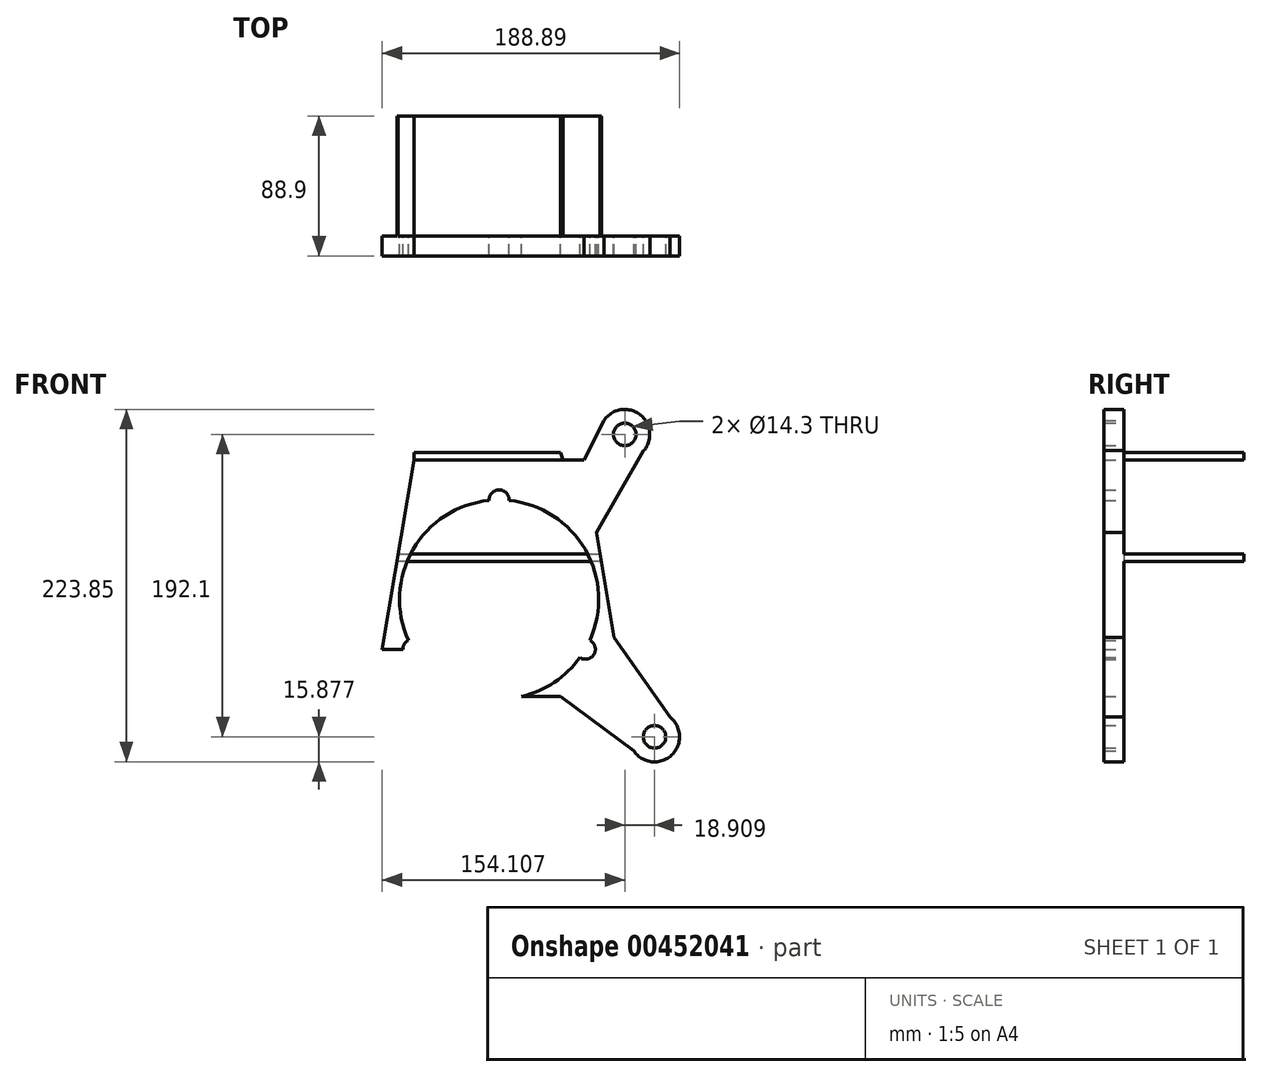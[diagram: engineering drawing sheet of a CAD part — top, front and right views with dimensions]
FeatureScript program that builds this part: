
annotation { "Feature Type Name" : "Feature", "Feature Type Description" : "" }
export const myFeature = defineFeature(function(context is Context, id is Id, definition is map)
    precondition{}
    {
        {
            var Q0;
            Q0=qCreatedBy(makeId("Front.planeOp"),FACE);
            var sketch = newSketch(context, id + "F0", { "sketchPlane" : qUnion([Q0])});
            skLineSegment(sketch, "E0", {"start": v(-53.98, 0) * mm, "end": v(53.98, 0) * mm});
            skLineSegment(sketch, "E1", {"start": v(-79.37, -150.27) * mm, "end": v(79.38, -150.27) * mm});
            skLineSegment(sketch, "E2", {"start": v(-53.97, 0) * mm, "end": v(-79.37, -150.27) * mm});
            skLineSegment(sketch, "E3", {"start": v(53.97, 0) * mm, "end": v(79.38, -150.27) * mm});
            skCircle(sketch, "E4", {"center": v(0, -25.4) * mm, "radius": 6.35 * mm});
            skCircle(sketch, "E5", {"center": v(-54.77, -120.26) * mm, "radius": 6.35 * mm});
            skCircle(sketch, "E6", {"center": v(54.77, -120.26) * mm, "radius": 6.35 * mm});
            skCircle(sketch, "E7", {"center": v(0, -88.67) * mm, "radius": 49.21 * mm});
            skLineSegment(sketch, "E8", {"start": v(-54.77, -120.26) * mm, "end": v(-156.37, -120.26) * mm});
            skLineSegment(sketch, "E9", {"start": v(0, -150.27) * mm, "end": v(0, -61.37) * mm});
            skLineSegment(sketch, "E10", {"start": v(-156.37, -120.26) * mm, "end": v(-156.37, -15.35) * mm});
            skCircle(sketch, "E11", {"center": v(0, -88.67) * mm, "radius": 131.75 * mm});
            skCircle(sketch, "E12", {"center": v(79.8, 16.17) * mm, "radius": 7.15 * mm});
            skCircle(sketch, "E13", {"center": v(98.72, -175.93) * mm, "radius": 7.15 * mm});
            skCircle(sketch, "E14", {"center": v(98.72, -175.93) * mm, "radius": 15.88 * mm});
            skCircle(sketch, "E15", {"center": v(79.8, 16.17) * mm, "radius": 15.88 * mm});
            skLineSegment(sketch, "E16", {"start": v(91.84, 5.8) * mm, "end": v(61.78, -46.18) * mm});
            skLineSegment(sketch, "E17", {"start": v(108.5, -163.43) * mm, "end": v(73.02, -112.66) * mm});
            skLineSegment(sketch, "E18", {"start": v(85.59, -184.86) * mm, "end": v(39.06, -150.27) * mm});
            skLineSegment(sketch, "E19", {"start": v(66.62, 25) * mm, "end": v(53.98, 0) * mm});
            skCircle(sketch, "E20", {"center": v(0, -88.67) * mm, "radius": 63.22 * mm});
            skSolve(sketch);
        }
        {
            var Q0;
            {var subQ5=sQuery(id+"F0.wireOp",EDGE,"E0");Q0=makeQuery(id+"F0.imprint","IMPRINT",FACE,{"disambiguationData":[TD([[makeQuery(id+"F0.imprint","IMPRINT",EDGE,{"derivedFrom":subQ5}),-1.0]])]});}
            var Q1;
            {var subQ3=sQuery(id+"F0.wireOp",EDGE,"E16");Q1=makeQuery(id+"F0.imprint","IMPRINT",FACE,{"disambiguationData":[TD([[makeQuery(id+"F0.imprint","IMPRINT",EDGE,{"derivedFrom":subQ3}),-1.0]])]});}
            var Q2;
            {var subQ0=sQuery(id+"F0.wireOp",EDGE,"E12");var subQ1=sQuery(id+"F0.wireOp",EDGE,"E11");var subQ2=makeQuery(id+"F0.imprint","INTERSECT",VERTEX,{"disambiguationData":[OD(0.0)],"derivedFrom":[subQ1,subQ0]});Q2=makeQuery(id+"F0.imprint","IMPRINT",FACE,{"disambiguationData":[TD([[makeQuery(id+"F0.imprint","IMPRINT",EDGE,{"disambiguationData":[TD([[subQ2,1.0]])],"derivedFrom":subQ0}),-1.0]])]});}
            var Q3;
            {var subQ1=sQuery(id+"F0.wireOp",EDGE,"E11");var subQ3=sQuery(id+"F0.wireOp",EDGE,"E12");var subQ4=makeQuery(id+"F0.imprint","INTERSECT",VERTEX,{"disambiguationData":[OD(0.0)],"derivedFrom":[subQ1,subQ3]});Q3=makeQuery(id+"F0.imprint","IMPRINT",FACE,{"disambiguationData":[TD([[makeQuery(id+"F0.imprint","IMPRINT",EDGE,{"disambiguationData":[TD([[subQ4,-1.0]])],"derivedFrom":subQ3}),-1.0]])]});}
            var Q4;
            {var subQ0=sQuery(id+"F0.wireOp",EDGE,"E17");Q4=makeQuery(id+"F0.imprint","IMPRINT",FACE,{"disambiguationData":[TD([[makeQuery(id+"F0.imprint","IMPRINT",EDGE,{"derivedFrom":subQ0}),1.0]])]});}
            var Q5;
            {var subQ0=sQuery(id+"F0.wireOp",EDGE,"E14");var subQ1=sQuery(id+"F0.wireOp",EDGE,"E11");var subQ7=makeQuery(id+"F0.imprint","INTERSECT",VERTEX,{"derivedFrom":[subQ1,subQ0]});Q5=makeQuery(id+"F0.imprint","IMPRINT",FACE,{"disambiguationData":[TD([[makeQuery(id+"F0.imprint","IMPRINT",EDGE,{"disambiguationData":[TD([[subQ7,-1.0]])],"derivedFrom":subQ1}),1.0]])]});}
            var Q6;
            {var subQ0=sQuery(id+"F0.wireOp",EDGE,"E14");var subQ1=sQuery(id+"F0.wireOp",EDGE,"E11");var subQ2=makeQuery(id+"F0.imprint","INTERSECT",VERTEX,{"derivedFrom":[subQ1,subQ0]});Q6=makeQuery(id+"F0.imprint","IMPRINT",FACE,{"disambiguationData":[TD([[makeQuery(id+"F0.imprint","IMPRINT",EDGE,{"disambiguationData":[TD([[subQ2,-1.0]])],"derivedFrom":subQ1}),-1.0]])]});}
            extrude(context, id + "F1", {"entities" : qUnion([Q0, Q1, Q2, Q3, Q4, Q5, Q6]), "depth" : 6.35 * mm, "hasSecondDirection" : true, "secondDirectionOppositeDirection" : true, "secondDirectionDepth" : 6.35 * mm});
        }
        {
            var Q0;
            Q0=makeQuery(id+"FOitl75tAzy8YSx_1.boolean.opBoolean","MERGE",FACE,{"derivedFrom":[makeQuery(id+"F1.opExtrude","CAP_FACE",FACE,{"disambiguationData":[OSD([sQuery(id+"F0.wireOp",EDGE,"E0"),sQuery(id+"F0.wireOp",EDGE,"E1"),sQuery(id+"F0.wireOp",EDGE,"E2"),sQuery(id+"F0.wireOp",EDGE,"E3"),sQuery(id+"F0.wireOp",EDGE,"E4"),sQuery(id+"F0.wireOp",EDGE,"E5"),sQuery(id+"F0.wireOp",EDGE,"E6"),sQuery(id+"F0.wireOp",EDGE,"E7"),sQuery(id+"F0.wireOp",EDGE,"E12"),sQuery(id+"F0.wireOp",EDGE,"E13"),sQuery(id+"F0.wireOp",EDGE,"E14"),sQuery(id+"F0.wireOp",EDGE,"E15"),sQuery(id+"F0.wireOp",EDGE,"E16"),sQuery(id+"F0.wireOp",EDGE,"E17"),sQuery(id+"F0.wireOp",EDGE,"E18"),sQuery(id+"F0.wireOp",EDGE,"E19")])],"isStart":true}),makeQuery(id+"FOitl75tAzy8YSx_1.opExtrude","SWEPT_FACE",FACE,{"disambiguationData":[OSD([sQuery(id+"FF2iT7GUfIGANON_1.wireOp",EDGE,"4CpptAuS-EF7Z-popT-YOGi-WrK1huyTGHxH.top")])]})]});
            var sketch = newSketch(context, id + "F2", { "sketchPlane" : qUnion([Q0])});
            skLineSegment(sketch, "E21.bottom", {"start": v(53.98, 0) * mm, "end": v(-39.06, 0) * mm});
            skLineSegment(sketch, "E21.top", {"start": v(53.98, 4.75) * mm, "end": v(-39.06, 4.75) * mm});
            skLineSegment(sketch, "E21.left", {"start": v(53.98, 0) * mm, "end": v(53.98, 4.75) * mm});
            skLineSegment(sketch, "E21.right", {"start": v(-39.06, 0) * mm, "end": v(-39.06, 4.75) * mm});
            skLineSegment(sketch, "E22", {"start": v(-39.06, 0) * mm, "end": v(-81.74, -125.14) * mm});
            skLineSegment(sketch, "E23", {"start": v(-81.74, -125.14) * mm, "end": v(-79.02, -121.24) * mm});
            skLineSegment(sketch, "E24", {"start": v(-79.02, -121.24) * mm, "end": v(-39.06, 4.75) * mm});
            skSolve(sketch);
        }
        {
            var Q0;
            Q0=makeQuery(id+"F2.imprint","IMPRINT",FACE,{"disambiguationData":[TD([[makeQuery(id+"F2.imprint","IMPRINT",EDGE,{"derivedFrom":sQuery(id+"F2.wireOp",EDGE,"E21.right")}),1.0]])]});
            var Q1;
            {var subQ0=sQuery(id+"F2.wireOp",EDGE,"E21.bottom");Q1=makeQuery(id+"F2.imprint","IMPRINT",FACE,{"disambiguationData":[TD([[makeQuery(id+"F2.imprint","IMPRINT",EDGE,{"derivedFrom":subQ0}),-1.0]])]});}
            extrude(context, id + "F3", {"entities" : qUnion([Q0, Q1]), "operationType" : NewBodyOperationType.ADD, "depth" : 76.2 * mm});
        }
        {
            var Q0;
            Q0=makeQuery(id+"F3.opExtrude","SWEPT_FACE",FACE,{"disambiguationData":[OSD([sQuery(id+"F2.wireOp",EDGE,"E21.top")])]});
            var sketch = newSketch(context, id + "F4", { "sketchPlane" : qUnion([Q0])});
            skCircle(sketch, "E25", {"center": v(0, 46.65) * mm, "radius": 9.53 * mm});
            skSolve(sketch);
        }
        {
            var Q0;
            Q0=sQuery(id+"F4.wireOp",VERTEX,"E25.center");
            var Q1;
            Q1=makeQuery(id+"F1.opExtrude","SWEPT_BODY",BODY,{"disambiguationData":[OSD([sQuery(id+"F0.wireOp",EDGE,"E0"),sQuery(id+"F0.wireOp",EDGE,"E1"),sQuery(id+"F0.wireOp",EDGE,"E2"),sQuery(id+"F0.wireOp",EDGE,"E3"),sQuery(id+"F0.wireOp",EDGE,"E4"),sQuery(id+"F0.wireOp",EDGE,"E5"),sQuery(id+"F0.wireOp",EDGE,"E6"),sQuery(id+"F0.wireOp",EDGE,"E7"),sQuery(id+"F0.wireOp",EDGE,"E12"),sQuery(id+"F0.wireOp",EDGE,"E13"),sQuery(id+"F0.wireOp",EDGE,"E14"),sQuery(id+"F0.wireOp",EDGE,"E15"),sQuery(id+"F0.wireOp",EDGE,"E16"),sQuery(id+"F0.wireOp",EDGE,"E17"),sQuery(id+"F0.wireOp",EDGE,"E18"),sQuery(id+"F0.wireOp",EDGE,"E19")])]});
            hole(context, id + "F5", {"style" : HoleStyle.SIMPLE, "endStyle" : HoleEndStyle.THROUGH, "holeDiameter" : 19.05 * mm, "isTappedThrough" : true, "tappedDepth" : 12.7 * mm, "tapClearance" : 3, "locations" : qUnion([Q0]), "scope" : qUnion([Q1])});
        }
        {
            var Q0;
            {var subQ0=sQuery(id+"F0.wireOp",EDGE,"E16");var subQ1=sQuery(id+"F0.wireOp",EDGE,"E15");var subQ2=sQuery(id+"F0.wireOp",EDGE,"E12");var subQ3=sQuery(id+"F0.wireOp",EDGE,"E7");var subQ5=sQuery(id+"F0.wireOp",EDGE,"E6");var subQ7=sQuery(id+"F0.wireOp",EDGE,"E17");var subQ8=sQuery(id+"F0.wireOp",EDGE,"E2");var subQ9=sQuery(id+"F0.wireOp",EDGE,"E3");var subQ10=sQuery(id+"F0.wireOp",EDGE,"E4");var subQ11=sQuery(id+"FF2iT7GUfIGANON_1.wireOp",EDGE,"4CpptAuS-EF7Z-popT-YOGi-WrK1huyTGHxH.top");var subQ12=sQuery(id+"F0.wireOp",EDGE,"E5");var subQ13=sQuery(id+"F0.wireOp",EDGE,"E19");Q0=makeQuery(id+"F3.boolean.opBoolean","SPLIT",FACE,{"disambiguationData":[TD([makeQuery(id+"F1.opExtrude","SWEPT_FACE",FACE,{"disambiguationData":[OSD([subQ8])]})])],"derivedFrom":makeQuery(id+"FOitl75tAzy8YSx_1.boolean.opBoolean","MERGE",FACE,{"derivedFrom":[makeQuery(id+"F1.opExtrude","CAP_FACE",FACE,{"disambiguationData":[OSD([sQuery(id+"F0.wireOp",EDGE,"E0"),sQuery(id+"F0.wireOp",EDGE,"E1"),subQ8,subQ9,subQ10,subQ12,subQ5,subQ3,subQ2,sQuery(id+"F0.wireOp",EDGE,"E13"),sQuery(id+"F0.wireOp",EDGE,"E14"),subQ1,subQ0,subQ7,sQuery(id+"F0.wireOp",EDGE,"E18"),subQ13])],"isStart":true}),makeQuery(id+"FOitl75tAzy8YSx_1.opExtrude","SWEPT_FACE",FACE,{"disambiguationData":[OSD([subQ11])]})]})});}
            var sketch = newSketch(context, id + "F6", { "sketchPlane" : qUnion([Q0])});
            skLineSegment(sketch, "E26", {"start": v(0, -64.57) * mm, "end": v(64.89, -64.57) * mm});
            skLineSegment(sketch, "E27", {"start": v(64.89, -64.57) * mm, "end": v(64.1, -59.89) * mm});
            skLineSegment(sketch, "E28", {"start": v(64.1, -59.89) * mm, "end": v(-64.1, -59.89) * mm});
            skLineSegment(sketch, "E29", {"start": v(-64.1, -59.89) * mm, "end": v(-64.89, -64.57) * mm});
            skLineSegment(sketch, "E30", {"start": v(-64.89, -64.57) * mm, "end": v(0, -64.57) * mm});
            skSolve(sketch);
        }
        {
            var Q0;
            {var subQ0=sQuery(id+"F6.wireOp",EDGE,"E26");var subQ6=sQuery(id+"F6.wireOp",EDGE,"E30");var subQ7=makeQuery(id+"F6.imprint","INTERSECT",VERTEX,{"derivedFrom":[subQ0,subQ6]});Q0=makeQuery(id+"F6.imprint","IMPRINT",FACE,{"disambiguationData":[TD([[makeQuery(id+"F6.imprint","IMPRINT",EDGE,{"disambiguationData":[TD([[subQ7,-1.0]])],"derivedFrom":subQ0}),1.0]])]});}
            var Q1;
            {var subQ0=sQuery(id+"F6.wireOp",EDGE,"E29");Q1=makeQuery(id+"F6.imprint","IMPRINT",FACE,{"disambiguationData":[TD([[makeQuery(id+"F6.imprint","IMPRINT",EDGE,{"derivedFrom":subQ0}),1.0]])]});}
            var Q2;
            {var subQ0=sQuery(id+"F6.wireOp",EDGE,"E27");Q2=makeQuery(id+"F6.imprint","IMPRINT",FACE,{"disambiguationData":[TD([[makeQuery(id+"F6.imprint","IMPRINT",EDGE,{"derivedFrom":subQ0}),-1.0]])]});}
            extrude(context, id + "F7", {"entities" : qUnion([Q0, Q1, Q2]), "operationType" : NewBodyOperationType.ADD, "depth" : 76.2 * mm});
        }
    });
